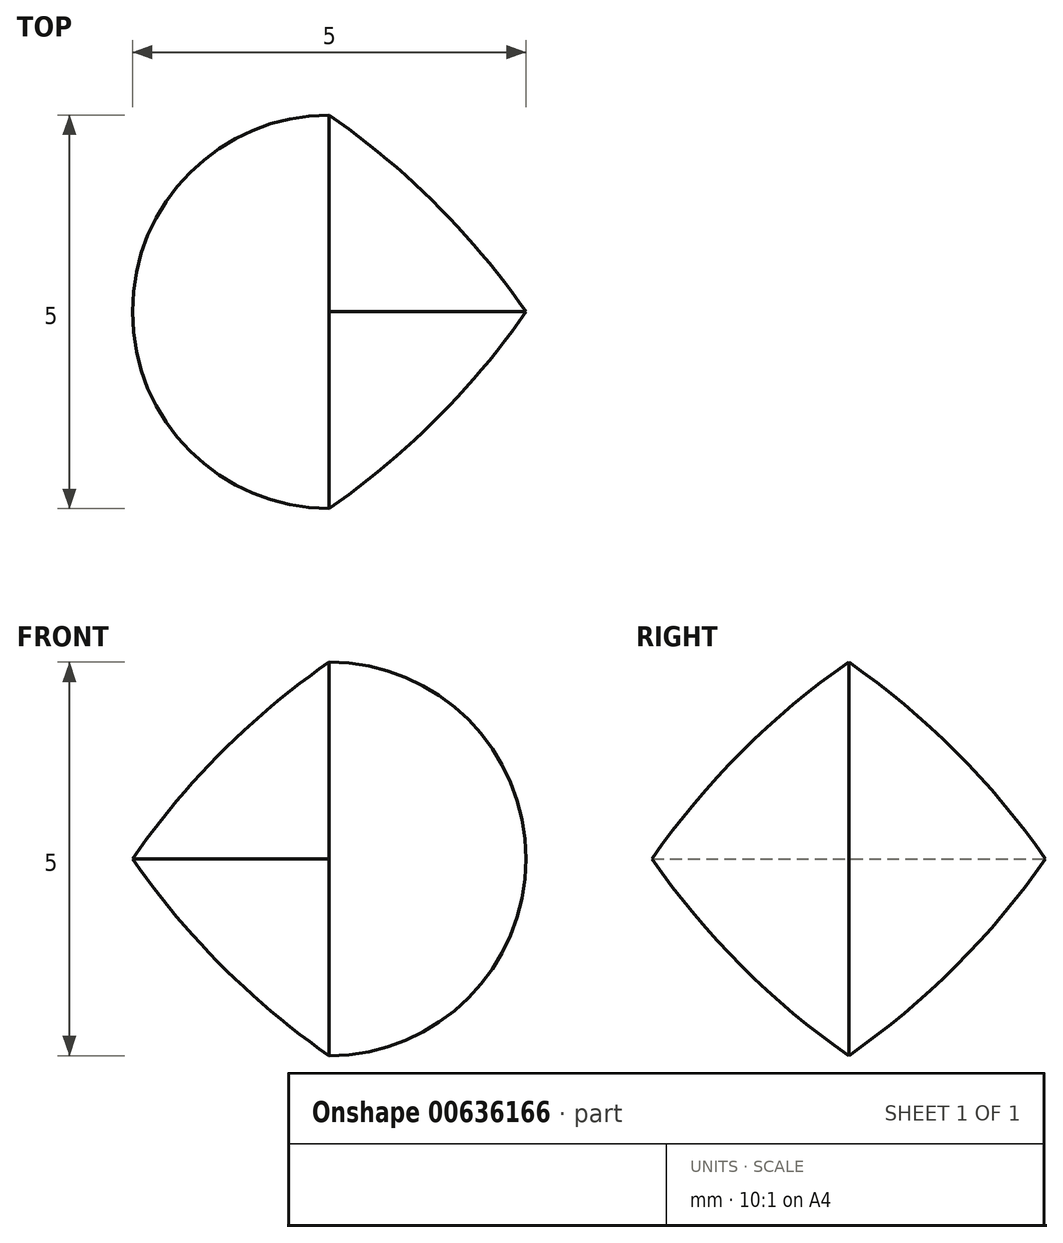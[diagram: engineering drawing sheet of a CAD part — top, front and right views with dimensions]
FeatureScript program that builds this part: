
annotation { "Feature Type Name" : "Feature", "Feature Type Description" : "" }
export const myFeature = defineFeature(function(context is Context, id is Id, definition is map)
    precondition{}
    {
        {
            var Q0;
            Q0=qCreatedBy(makeId("Right.planeOp"),FACE);
            var sketch = newSketch(context, id + "F0", { "sketchPlane" : qUnion([Q0])});
            skLineSegment(sketch, "E0", {"start": v(0, 0) * mm, "end": v(2.5, 0) * mm});
            skLineSegment(sketch, "E1", {"start": v(0, 0) * mm, "end": v(0, 2.5) * mm});
            skArc(sketch, "E2", {"start": v(2.5, 0) * mm, "mid": v(1.36, 1.36) * mm, "end": v(0, 2.5) * mm});
            skSolve(sketch);
        }
        {
            var Q0;
            Q0=qCreatedBy(makeId("Top.planeOp"),FACE);
            var sketch = newSketch(context, id + "F1", { "sketchPlane" : qUnion([Q0])});
            skCircle(sketch, "E3", {"center": v(0, 0) * mm, "radius": 1.36 * mm, "construction": true});
            skLineSegment(sketch, "E4", {"start": v(0, 0) * mm, "end": v(7.96, 0) * mm, "construction": true});
            skSolve(sketch);
        }
        {
            var Q0;
            Q0=makeQuery(id+"F0.imprint","IMPRINT",FACE,{"disambiguationData":[TD([[makeQuery(id+"F0.imprint","IMPRINT",EDGE,{"derivedFrom":sQuery(id+"F0.wireOp",EDGE,"E0")}),1.0]])]});
            var Q1;
            Q1=sQuery(id+"F0.wireOp",EDGE,"E1");
            revolve(context, id + "F2", {"surfaceOperationType" : NewSurfaceOperationType.NEW, "entities" : qUnion([Q0]), "axis" : qUnion([Q1]), "revolveType" : RevolveType.ONE_DIRECTION, "angle" : 180 * degree});
        }
        {
            var Q0;
            Q0=makeQuery(id+"F2.opRevolve","SWEPT_BODY",BODY,{"disambiguationData":[OSD([sQuery(id+"F0.wireOp",EDGE,"E0"),sQuery(id+"F0.wireOp",EDGE,"E1"),sQuery(id+"F0.wireOp",EDGE,"E2")])]});
            var Q1;
            Q1=makeQuery(id+"F2.opRevolve","SWEPT_FACE",FACE,{"disambiguationData":[OSD([sQuery(id+"F0.wireOp",EDGE,"E0")])]});
            mirror(context, id + "F3", {"operationType" : NewBodyOperationType.ADD, "entities" : qUnion([Q0]), "mirrorPlane" : qUnion([Q1])});
        }
        {
            var Q0;
            Q0=makeQuery(id+"F2.opRevolve","SWEPT_BODY",BODY,{"disambiguationData":[OSD([sQuery(id+"F0.wireOp",EDGE,"E0"),sQuery(id+"F0.wireOp",EDGE,"E1"),sQuery(id+"F0.wireOp",EDGE,"E2")])]});
            var Q1;
            {var subQ0=makeQuery(id+"F2.opRevolve","CAP_FACE",FACE,{"disambiguationData":[OSD([sQuery(id+"F0.wireOp",EDGE,"E0"),sQuery(id+"F0.wireOp",EDGE,"E1"),sQuery(id+"F0.wireOp",EDGE,"E2")])],"isStart":false});Q1=makeQuery(id+"F3.boolean.opBoolean","MERGE",FACE,{"derivedFrom":[subQ0,makeQuery(id+"F3.opPattern","COPY",FACE,{"derivedFrom":subQ0,"instanceName":"1"})]});}
            mirror(context, id + "F4", {"entities" : qUnion([Q0]), "mirrorPlane" : qUnion([Q1])});
        }
        {
            var Q0;
            Q0=makeQuery(id+"F4.opPattern","COPY",BODY,{"derivedFrom":makeQuery(id+"F2.opRevolve","SWEPT_BODY",BODY,{"disambiguationData":[OSD([sQuery(id+"F0.wireOp",EDGE,"E0"),sQuery(id+"F0.wireOp",EDGE,"E1"),sQuery(id+"F0.wireOp",EDGE,"E2")])]}),"instanceName":"1"});
            var Q1;
            Q1=sQuery(id+"F1.wireOp",EDGE,"E4");
            transform(context, id + "F5", {"entities" : qUnion([Q0]), "transformType" : TransformType.ROTATION, "transformAxis" : qUnion([Q1]), "angle" : 90 * degree, "makeCopy" : false});
        }
    });
